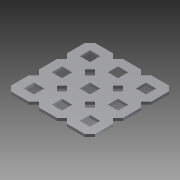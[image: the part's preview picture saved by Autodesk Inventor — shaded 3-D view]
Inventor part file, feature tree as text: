
AUTODESK INVENTOR PART (.ipt)
format: ipt  version: 2014 SP1 (Build 180222100, 222)  size: 498,176 bytes
history: native  units: in
note: dims shown in document units (in); Inventor stores cm internally (conversion verified against a paired STEP export)
features: other x1, imported_body x1, extrude x1, sketch x1
ambient origin geometry x8: Origin, YZ Plane, XZ Plane, XY Plane, X Axis, Y Axis, Z Axis, Center Point
bodies: Body1 (feature_tree)
feature tree (4):
  parser-record x1  (decoder bookkeeping rows leaked as tree rows — omitted from the tree; the rows remain in map.json)
  imported_body  "Base1"
  extrude  "Extrusion1"  Depth=1.5in
  sketch  "Sketch1"  dims[d0=1.5in d1=1.5in d2=1.0in d3=0.0in]
